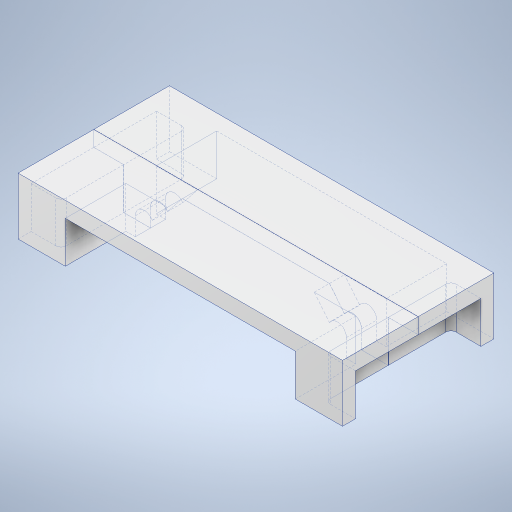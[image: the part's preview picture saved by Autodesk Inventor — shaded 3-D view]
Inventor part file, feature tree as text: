
AUTODESK INVENTOR PART (.ipt)
format: ipt  version: 2024 (Build 280153000, 153)  size: 409,600 bytes
history: native  units: mm
features: sketch x7, extrude x6, projected_geometry x5, fillet x1
ambient origin geometry x8: Origin, YZ Plane, XZ Plane, XY Plane, X Axis, Y Axis, Z Axis, Center Point
bodies: Solid1 (feature_tree)
feature tree (19):
  extrude  "Extrusion1"  Depth=175.0mm
  extrude  "Extrusion2"  Depth=18.0mm TaperAngle=0.0deg
  extrude  "Extrusion3"  Depth=265.893mm
  fillet  "Fillet1"  Radius=265.893mm
  sketch  "Sketch4"  dims[d11=20.0mm d12=20.0mm]
  extrude  "Extrusion4"  Depth=20.0mm
  extrude  "Extrusion5"  Depth=34.5535mm
  extrude  "Extrusion6"  Depth=15.0mm
  sketch  "Sketch1"  dims[d0=175.0mm d1=175.0mm]
  sketch  "Sketch2"  dims[d2=12.0mm d3=0.0mm d6=18.0mm d7=0.0mm]
  sketch  "Sketch3"  dims[d8=100.0mm d9=100.0mm d10=265.893mm]
  projected_geometry  "Projected Loop1"
  sketch  "Sketch5"  dims[d13=34.5535mm d14=34.5535mm]
  sketch  "Sketch6"  dims[d15=48.0mm d16=0.0mm d17=15.0mm]
  sketch  "Sketch7"  dims[d18=15.0mm d19=15.0mm d20=15.0mm d21=6.0mm d22=50.0mm d23=50.0mm d24=70.0mm d25=70.0mm d26=223.0mm d27=21.4465mm d29=26.925mm d30=26.925mm d31=21.4465mm d32=21.0mm d33=21.0mm d34=12.0mm d35=2.0mm d37=2.0mm d38=54.0mm d39=0.0mm d40=5.0mm d41=5.0mm d42=87.45mm d43=87.45mm d44=98.0mm d45=0.0mm d46=6.0mm d47=0.0mm]
  projected_geometry  "Projected Loop2"
  projected_geometry  "Projected Loop3"
  projected_geometry  "Projected Loop4"
  projected_geometry  "Projected Loop5"
